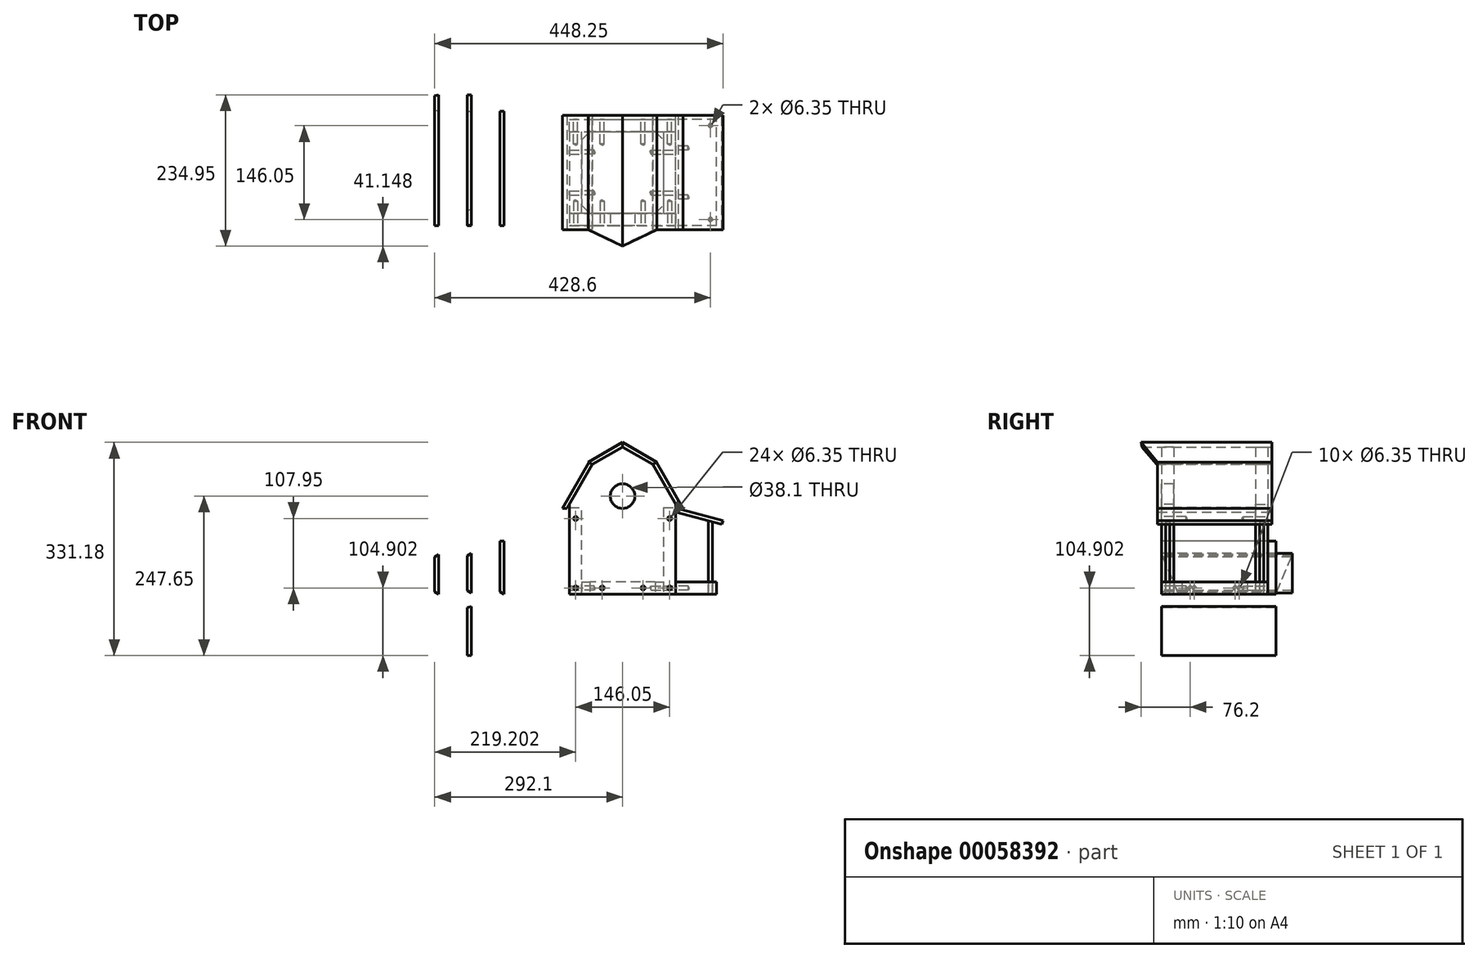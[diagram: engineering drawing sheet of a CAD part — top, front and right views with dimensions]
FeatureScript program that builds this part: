
annotation { "Feature Type Name" : "Feature", "Feature Type Description" : "" }
export const myFeature = defineFeature(function(context is Context, id is Id, definition is map)
    precondition{}
    {
        {
            var Q0;
            Q0=qCreatedBy(makeId("Front.planeOp"),FACE);
            var sketch = newSketch(context, id + "F0", { "sketchPlane" : qUnion([Q0])});
            skLineSegment(sketch, "E0", {"start": v(0, 0) * mm, "end": v(0, 139.7) * mm});
            skLineSegment(sketch, "E1", {"start": v(0, 139.7) * mm, "end": v(35.71, 201.56) * mm});
            skLineSegment(sketch, "E2", {"start": v(35.71, 201.56) * mm, "end": v(82.55, 228.6) * mm});
            skLineSegment(sketch, "E3", {"start": v(129.39, 201.56) * mm, "end": v(165.1, 139.7) * mm});
            skLineSegment(sketch, "E4", {"start": v(165.1, 139.7) * mm, "end": v(165.1, 0) * mm});
            skLineSegment(sketch, "E5", {"start": v(165.1, 0) * mm, "end": v(0, 0) * mm});
            skLineSegment(sketch, "E6", {"start": v(82.55, 0) * mm, "end": v(82.55, 304.8) * mm, "construction": true});
            skLineSegment(sketch, "E7", {"start": v(82.55, 228.6) * mm, "end": v(129.39, 201.56) * mm});
            skLineSegment(sketch, "E8", {"start": v(-28.74, 228.6) * mm, "end": v(153.15, 228.6) * mm, "construction": true});
            skCircle(sketch, "E9", {"center": v(82.55, 152.4) * mm, "radius": 19.05 * mm});
            skCircle(sketch, "E10", {"center": v(9.65, 9.65) * mm, "radius": 3.18 * mm});
            skCircle(sketch, "E11", {"center": v(50.8, 9.65) * mm, "radius": 3.17 * mm});
            skCircle(sketch, "E12", {"center": v(114.43, 9.65) * mm, "radius": 3.18 * mm});
            skCircle(sketch, "E13", {"center": v(155.7, 9.65) * mm, "radius": 3.18 * mm});
            skCircle(sketch, "E14", {"center": v(9.65, 117.6) * mm, "radius": 3.18 * mm});
            skCircle(sketch, "E15", {"center": v(155.7, 117.6) * mm, "radius": 3.18 * mm});
            skLineSegment(sketch, "E16.bottom", {"start": v(9.65, 9.65) * mm, "end": v(155.7, 9.65) * mm, "construction": true});
            skLineSegment(sketch, "E16.top", {"start": v(9.65, 117.6) * mm, "end": v(155.7, 117.6) * mm, "construction": true});
            skLineSegment(sketch, "E16.left", {"start": v(9.65, 9.65) * mm, "end": v(9.65, 117.6) * mm, "construction": true});
            skLineSegment(sketch, "E16.right", {"start": v(155.7, 9.65) * mm, "end": v(155.7, 117.6) * mm, "construction": true});
            skSolve(sketch);
        }
        {
            var Q0;
            Q0=makeQuery(id+"F0.imprint","IMPRINT",FACE,{"disambiguationData":[TD([[makeQuery(id+"F0.imprint","IMPRINT",EDGE,{"derivedFrom":sQuery(id+"F0.wireOp",EDGE,"E0")}),-1.0]])]});
            extrude(context, id + "F1", {"entities" : qUnion([Q0]), "oppositeDirection" : true, "depth" : 19.05 * mm});
        }
        {
            var Q0;
            Q0=makeQuery(id+"F1.opExtrude","SWEPT_EDGE",EDGE,{"disambiguationData":[OSD([sQuery(id+"F0.wireOp",EDGE,"E2"),sQuery(id+"F0.wireOp",EDGE,"E7")])]});
            cPlane(context, id + "F2", {"entities" : qUnion([Q0]), "cplaneType" : CPlaneType.LINE_ANGLE, "offset" : 152.4 * mm, "angle" : 90 * degree, "width" : 152.4 * mm, "height" : 152.4 * mm});
        }
        {
            var Q0;
            Q0=qCreatedBy(makeId("Front.planeOp"),FACE);
            cPlane(context, id + "F3", {"entities" : qUnion([Q0]), "cplaneType" : CPlaneType.OFFSET, "offset" : 165.1 * mm, "oppositeDirection" : true, "width" : 152.4 * mm, "height" : 152.4 * mm});
        }
        {
            var Q0;
            Q0=qCreatedBy(id+"F3.planeOp",FACE);
            var sketch = newSketch(context, id + "F4", { "sketchPlane" : qUnion([Q0])});
            skLineSegment(sketch, "E17", {"start": v(0, 0) * mm, "end": v(0, 139.7) * mm});
            skLineSegment(sketch, "E18", {"start": v(0, 139.7) * mm, "end": v(35.71, 201.56) * mm});
            skLineSegment(sketch, "E19", {"start": v(35.71, 201.56) * mm, "end": v(82.55, 228.6) * mm});
            skLineSegment(sketch, "E20", {"start": v(82.55, 228.6) * mm, "end": v(129.39, 201.56) * mm});
            skLineSegment(sketch, "E21", {"start": v(129.39, 201.56) * mm, "end": v(165.1, 139.7) * mm});
            skLineSegment(sketch, "E22", {"start": v(0, 0) * mm, "end": v(165.1, 0) * mm});
            skLineSegment(sketch, "E23", {"start": v(165.1, 139.7) * mm, "end": v(165.1, 0) * mm});
            skCircle(sketch, "E24", {"center": v(9.65, 9.65) * mm, "radius": 3.18 * mm});
            skCircle(sketch, "E25", {"center": v(50.8, 9.65) * mm, "radius": 3.18 * mm});
            skCircle(sketch, "E26", {"center": v(114.43, 9.65) * mm, "radius": 3.18 * mm});
            skCircle(sketch, "E27", {"center": v(155.7, 9.65) * mm, "radius": 3.18 * mm});
            skCircle(sketch, "E28", {"center": v(155.7, 117.6) * mm, "radius": 3.18 * mm});
            skCircle(sketch, "E29", {"center": v(9.65, 117.6) * mm, "radius": 3.18 * mm});
            skLineSegment(sketch, "E30.bottom", {"start": v(155.7, 9.65) * mm, "end": v(9.65, 9.65) * mm, "construction": true});
            skLineSegment(sketch, "E30.top", {"start": v(155.7, 117.6) * mm, "end": v(9.65, 117.6) * mm, "construction": true});
            skLineSegment(sketch, "E30.left", {"start": v(155.7, 9.65) * mm, "end": v(155.7, 117.6) * mm, "construction": true});
            skLineSegment(sketch, "E30.right", {"start": v(9.65, 9.65) * mm, "end": v(9.65, 117.6) * mm, "construction": true});
            skSolve(sketch);
        }
        {
            var Q0;
            Q0=makeQuery(id+"F4.imprint","IMPRINT",FACE,{"disambiguationData":[TD([[makeQuery(id+"F4.imprint","IMPRINT",EDGE,{"derivedFrom":sQuery(id+"F4.wireOp",EDGE,"E17")}),-1.0]])]});
            extrude(context, id + "F5", {"entities" : qUnion([Q0]), "depth" : 19.05 * mm});
        }
        {
            var Q0;
            Q0=qCreatedBy(makeId("Top.planeOp"),FACE);
            var sketch = newSketch(context, id + "F6", { "sketchPlane" : qUnion([Q0])});
            skLineSegment(sketch, "E31", {"start": v(19.05, 133.35) * mm, "end": v(19.05, 31.75) * mm});
            skLineSegment(sketch, "E32", {"start": v(146.05, 133.35) * mm, "end": v(146.05, 31.75) * mm});
            skLineSegment(sketch, "E33", {"start": v(82.55, -58.96) * mm, "end": v(82.55, 162.28) * mm, "construction": true});
            skLineSegment(sketch, "E34", {"start": v(133.35, 19.05) * mm, "end": v(31.75, 19.05) * mm});
            skLineSegment(sketch, "E35", {"start": v(133.35, 146.05) * mm, "end": v(31.75, 146.05) * mm});
            skLineSegment(sketch, "E36", {"start": v(19.05, 31.75) * mm, "end": v(31.75, 19.05) * mm});
            skLineSegment(sketch, "E37", {"start": v(133.35, 19.05) * mm, "end": v(146.05, 31.75) * mm});
            skLineSegment(sketch, "E38", {"start": v(133.35, 146.05) * mm, "end": v(146.05, 133.35) * mm});
            skLineSegment(sketch, "E39", {"start": v(19.05, 133.35) * mm, "end": v(31.75, 146.05) * mm});
            skSolve(sketch);
        }
        {
            var Q0;
            Q0=makeQuery(id+"F6.imprint","IMPRINT",FACE,{"disambiguationData":[TD([[makeQuery(id+"F6.imprint","IMPRINT",EDGE,{"derivedFrom":sQuery(id+"F6.wireOp",EDGE,"E31")}),1.0]])]});
            var Q1;
            Q1=makeQuery(id+"F5.opExtrude","SWEPT_FACE",FACE,{"disambiguationData":[OSD([sQuery(id+"F4.wireOp",EDGE,"E22")])]});
            extrude(context, id + "F7", {"entities" : qUnion([Q0]), "endBoundEntityFace" : qUnion([Q1]), "depth" : 19.05 * mm});
        }
        {
            var Q0;
            Q0=makeQuery(id+"F7.opExtrude","SWEPT_FACE",FACE,{"disambiguationData":[OSD([sQuery(id+"F6.wireOp",EDGE,"E32")])]});
            var sketch = newSketch(context, id + "F8", { "sketchPlane" : qUnion([Q0])});
            skPoint(sketch, "E40", {"position": v(50.8, 9.65) * mm});
            skPoint(sketch, "E41", {"position": v(114.3, 9.65) * mm});
            skSolve(sketch);
        }
        {
            var Q0;
            Q0=makeQuery(id+"F7.opExtrude","SWEPT_FACE",FACE,{"disambiguationData":[OSD([sQuery(id+"F6.wireOp",EDGE,"E34")])]});
            var sketch = newSketch(context, id + "F9", { "sketchPlane" : qUnion([Q0])});
            skPoint(sketch, "E42", {"position": v(50.8, 9.65) * mm});
            skPoint(sketch, "E43", {"position": v(114.3, 9.65) * mm});
            skSolve(sketch);
        }
        {
            var Q0;
            Q0=makeQuery(id+"F7.opExtrude","SWEPT_FACE",FACE,{"disambiguationData":[OSD([sQuery(id+"F6.wireOp",EDGE,"E31")])]});
            var sketch = newSketch(context, id + "F10", { "sketchPlane" : qUnion([Q0])});
            skPoint(sketch, "E44", {"position": v(-114.3, 9.65) * mm});
            skPoint(sketch, "E45", {"position": v(-50.8, 9.65) * mm});
            skSolve(sketch);
        }
        {
            var Q0;
            Q0=makeQuery(id+"F7.opExtrude","SWEPT_FACE",FACE,{"disambiguationData":[OSD([sQuery(id+"F6.wireOp",EDGE,"E35")])]});
            var sketch = newSketch(context, id + "F11", { "sketchPlane" : qUnion([Q0])});
            skPoint(sketch, "E46", {"position": v(-114.3, 9.65) * mm});
            skPoint(sketch, "E47", {"position": v(-50.8, 9.65) * mm});
            skSolve(sketch);
        }
        {
            var Q0;
            Q0=sQuery(id+"F11.wireOp",VERTEX,"E46");
            var Q1;
            Q1=sQuery(id+"F11.wireOp",VERTEX,"E47");
            var Q2;
            Q2=sQuery(id+"F10.wireOp",VERTEX,"E44");
            var Q3;
            Q3=sQuery(id+"F10.wireOp",VERTEX,"E45");
            var Q4;
            Q4=sQuery(id+"F9.wireOp",VERTEX,"E42");
            var Q5;
            Q5=sQuery(id+"F9.wireOp",VERTEX,"E43");
            var Q6;
            Q6=sQuery(id+"F8.wireOp",VERTEX,"E40");
            var Q7;
            Q7=sQuery(id+"F8.wireOp",VERTEX,"E41");
            var Q8;
            Q8=makeQuery(id+"F7.opExtrude","SWEPT_BODY",BODY,{"disambiguationData":[OSD([sQuery(id+"F6.wireOp",EDGE,"E31"),sQuery(id+"F6.wireOp",EDGE,"E32"),sQuery(id+"F6.wireOp",EDGE,"E34"),sQuery(id+"F6.wireOp",EDGE,"E35"),sQuery(id+"F6.wireOp",EDGE,"E36"),sQuery(id+"F6.wireOp",EDGE,"E37"),sQuery(id+"F6.wireOp",EDGE,"E38"),sQuery(id+"F6.wireOp",EDGE,"E39")])]});
            hole(context, id + "F12", {"style" : HoleStyle.SIMPLE, "holeDiameter" : 6.35 * mm, "endStyle" : HoleEndStyle.BLIND, "holeDepth" : 19.05 * mm, "locations" : qUnion([Q0, Q1, Q2, Q3, Q4, Q5, Q6, Q7]), "scope" : qUnion([Q8])});
        }
        {
            var Q0;
            Q0=qCreatedBy(makeId("Right.planeOp"),FACE);
            cPlane(context, id + "F13", {"entities" : qUnion([Q0]), "cplaneType" : CPlaneType.OFFSET, "offset" : 165.1 * mm, "width" : 152.4 * mm, "height" : 152.4 * mm});
        }
        {
            var Q0;
            Q0=qCreatedBy(id+"F13.planeOp",FACE);
            var sketch = newSketch(context, id + "F14", { "sketchPlane" : qUnion([Q0])});
            skLineSegment(sketch, "E48.bottom", {"start": v(19.05, 0) * mm, "end": v(146.05, 0) * mm});
            skLineSegment(sketch, "E48.top", {"start": v(19.05, 134.87) * mm, "end": v(146.05, 134.87) * mm});
            skLineSegment(sketch, "E48.left", {"start": v(19.05, 0) * mm, "end": v(19.05, 134.87) * mm});
            skLineSegment(sketch, "E48.right", {"start": v(146.05, 0) * mm, "end": v(146.05, 134.87) * mm});
            skCircle(sketch, "E49", {"center": v(50.8, 9.65) * mm, "radius": 3.18 * mm});
            skCircle(sketch, "E50", {"center": v(114.3, 9.65) * mm, "radius": 3.18 * mm});
            skLineSegment(sketch, "E51", {"start": v(-9.39, 9.65) * mm, "end": v(175.82, 9.65) * mm, "construction": true});
            skSolve(sketch);
        }
        {
            var Q0;
            Q0=makeQuery(id+"F14.imprint","IMPRINT",FACE,{"disambiguationData":[TD([[makeQuery(id+"F14.imprint","IMPRINT",EDGE,{"derivedFrom":sQuery(id+"F14.wireOp",EDGE,"E48.bottom")}),1.0]])]});
            var Q1;
            Q1=makeQuery(id+"F7.opExtrude","SWEPT_FACE",FACE,{"disambiguationData":[OSD([sQuery(id+"F6.wireOp",EDGE,"E32")])]});
            extrude(context, id + "F15", {"entities" : qUnion([Q0]), "endBound" : BoundingType.UP_TO_SURFACE, "oppositeDirection" : true, "endBoundEntityFace" : qUnion([Q1]), "depth" : 25.4 * mm});
        }
        {
            var Q0;
            Q0=makeQuery(id+"F15.opExtrude","SWEPT_BODY",BODY,{"disambiguationData":[OSD([sQuery(id+"F14.wireOp",EDGE,"E48.bottom"),sQuery(id+"F14.wireOp",EDGE,"E48.top"),sQuery(id+"F14.wireOp",EDGE,"E48.left"),sQuery(id+"F14.wireOp",EDGE,"E48.right")])]});
            transform(context, id + "F16", {"entities" : qUnion([Q0]), "transformType" : TransformType.TRANSLATION_3D, "dx" : -146.05 * mm, "dy" : 0 * mm, "dz" : 0 * mm, "makeCopy" : true});
        }
        {
            var Q0;
            Q0=makeQuery(id+"F15.opExtrude","SWEPT_FACE",FACE,{"disambiguationData":[OSD([sQuery(id+"F14.wireOp",EDGE,"E48.left")])]});
            var sketch = newSketch(context, id + "F17", { "sketchPlane" : qUnion([Q0])});
            skPoint(sketch, "E52", {"position": v(155.45, 117.6) * mm});
            skPoint(sketch, "E53", {"position": v(9.65, 117.6) * mm});
            skPoint(sketch, "E54", {"position": v(9.65, 9.65) * mm});
            skPoint(sketch, "E55", {"position": v(155.45, 9.65) * mm});
            skSolve(sketch);
        }
        {
            var Q0;
            Q0=sQuery(id+"F17.wireOp",VERTEX,"E53");
            var Q1;
            Q1=sQuery(id+"F17.wireOp",VERTEX,"E52");
            var Q2;
            Q2=sQuery(id+"F17.wireOp",VERTEX,"E54");
            var Q3;
            Q3=sQuery(id+"F17.wireOp",VERTEX,"E55");
            var Q4;
            Q4=makeQuery(id+"F16.opPattern","COPY",BODY,{"derivedFrom":makeQuery(id+"F15.opExtrude","SWEPT_BODY",BODY,{"disambiguationData":[OSD([sQuery(id+"F14.wireOp",EDGE,"E48.bottom"),sQuery(id+"F14.wireOp",EDGE,"E48.top"),sQuery(id+"F14.wireOp",EDGE,"E48.left"),sQuery(id+"F14.wireOp",EDGE,"E48.right"),sQuery(id+"F14.wireOp",EDGE,"E49"),sQuery(id+"F14.wireOp",EDGE,"E50")])]}),"instanceName":"1"});
            var Q5;
            Q5=makeQuery(id+"F15.opExtrude","SWEPT_BODY",BODY,{"disambiguationData":[OSD([sQuery(id+"F14.wireOp",EDGE,"E48.bottom"),sQuery(id+"F14.wireOp",EDGE,"E48.top"),sQuery(id+"F14.wireOp",EDGE,"E48.left"),sQuery(id+"F14.wireOp",EDGE,"E48.right"),sQuery(id+"F14.wireOp",EDGE,"E49"),sQuery(id+"F14.wireOp",EDGE,"E50")])]});
            hole(context, id + "F18", {"style" : HoleStyle.SIMPLE, "holeDiameter" : 6.35 * mm, "endStyle" : HoleEndStyle.BLIND, "holeDepth" : 19.05 * mm, "locations" : qUnion([Q0, Q1, Q2, Q3]), "scope" : qUnion([Q4, Q5])});
        }
        {
            var Q0;
            Q0=makeQuery(id+"F15.opExtrude","SWEPT_FACE",FACE,{"disambiguationData":[OSD([sQuery(id+"F14.wireOp",EDGE,"E48.right")])]});
            var sketch = newSketch(context, id + "F19", { "sketchPlane" : qUnion([Q0])});
            skPoint(sketch, "E56", {"position": v(-155.45, 117.6) * mm});
            skPoint(sketch, "E57", {"position": v(-9.65, 117.6) * mm});
            skPoint(sketch, "E58", {"position": v(-9.65, 9.65) * mm});
            skPoint(sketch, "E59", {"position": v(-155.45, 9.65) * mm});
            skSolve(sketch);
        }
        {
            var Q0;
            Q0=sQuery(id+"F19.wireOp",VERTEX,"E56");
            var Q1;
            Q1=sQuery(id+"F19.wireOp",VERTEX,"E57");
            var Q2;
            Q2=sQuery(id+"F19.wireOp",VERTEX,"E58");
            var Q3;
            Q3=sQuery(id+"F19.wireOp",VERTEX,"E59");
            var Q4;
            Q4=makeQuery(id+"F15.opExtrude","SWEPT_BODY",BODY,{"disambiguationData":[OSD([sQuery(id+"F14.wireOp",EDGE,"E48.bottom"),sQuery(id+"F14.wireOp",EDGE,"E48.top"),sQuery(id+"F14.wireOp",EDGE,"E48.left"),sQuery(id+"F14.wireOp",EDGE,"E48.right"),sQuery(id+"F14.wireOp",EDGE,"E49"),sQuery(id+"F14.wireOp",EDGE,"E50")])]});
            var Q5;
            Q5=makeQuery(id+"F16.opPattern","COPY",BODY,{"derivedFrom":makeQuery(id+"F15.opExtrude","SWEPT_BODY",BODY,{"disambiguationData":[OSD([sQuery(id+"F14.wireOp",EDGE,"E48.bottom"),sQuery(id+"F14.wireOp",EDGE,"E48.top"),sQuery(id+"F14.wireOp",EDGE,"E48.left"),sQuery(id+"F14.wireOp",EDGE,"E48.right"),sQuery(id+"F14.wireOp",EDGE,"E49"),sQuery(id+"F14.wireOp",EDGE,"E50")])]}),"instanceName":"1"});
            hole(context, id + "F20", {"style" : HoleStyle.SIMPLE, "holeDiameter" : 6.35 * mm, "endStyle" : HoleEndStyle.BLIND, "holeDepth" : 19.05 * mm, "locations" : qUnion([Q0, Q1, Q2, Q3]), "scope" : qUnion([Q4, Q5])});
        }
        {
            var Q0;
            Q0=makeQuery(id+"F1.opExtrude","CAP_FACE",FACE,{"disambiguationData":[OSD([sQuery(id+"F0.wireOp",EDGE,"E0"),sQuery(id+"F0.wireOp",EDGE,"E1"),sQuery(id+"F0.wireOp",EDGE,"E2"),sQuery(id+"F0.wireOp",EDGE,"E3"),sQuery(id+"F0.wireOp",EDGE,"E4"),sQuery(id+"F0.wireOp",EDGE,"E5"),sQuery(id+"F0.wireOp",EDGE,"E7"),sQuery(id+"F0.wireOp",EDGE,"E9")])],"isStart":true});
            var sketch = newSketch(context, id + "F21", { "sketchPlane" : qUnion([Q0])});
            skLineSegment(sketch, "E60", {"start": v(82.55, 228.6) * mm, "end": v(82.55, 235.93) * mm});
            skLineSegment(sketch, "E61", {"start": v(135.74, 205.23) * mm, "end": v(129.39, 201.56) * mm});
            skLineSegment(sketch, "E62", {"start": v(129.39, 201.56) * mm, "end": v(82.55, 228.6) * mm});
            skLineSegment(sketch, "E63", {"start": v(82.55, 235.93) * mm, "end": v(135.74, 205.23) * mm});
            skSolve(sketch);
        }
        {
            var Q0;
            Q0=makeQuery(id+"F21.imprint","IMPRINT",FACE,{"disambiguationData":[TD([[makeQuery(id+"F21.imprint","IMPRINT",EDGE,{"derivedFrom":sQuery(id+"F21.wireOp",EDGE,"E60")}),-1.0]])]});
            extrude(context, id + "F22", {"entities" : qUnion([Q0]), "depth" : 31.75 * mm, "hasSecondDirection" : true, "secondDirectionOppositeDirection" : true, "secondDirectionDepth" : 171.45 * mm});
        }
        {
            var Q0;
            Q0=makeQuery(id+"F22.opExtrude","SWEPT_FACE",FACE,{"disambiguationData":[OSD([sQuery(id+"F21.wireOp",EDGE,"E63")])]});
            var sketch = newSketch(context, id + "F23", { "sketchPlane" : qUnion([Q0])});
            skLineSegment(sketch, "E64", {"start": v(-46.48, -31.75) * mm, "end": v(14.94, -31.75) * mm});
            skLineSegment(sketch, "E65", {"start": v(14.94, -31.75) * mm, "end": v(14.94, -6.31) * mm});
            skLineSegment(sketch, "E66", {"start": v(14.94, -6.31) * mm, "end": v(-46.48, -31.75) * mm});
            skSolve(sketch);
        }
        {
            var Q0;
            Q0=makeQuery(id+"F23.imprint","IMPRINT",FACE,{"disambiguationData":[TD([[makeQuery(id+"F23.imprint","IMPRINT",EDGE,{"derivedFrom":sQuery(id+"F23.wireOp",EDGE,"E64")}),1.0]])]});
            extrude(context, id + "F24", {"entities" : qUnion([Q0]), "operationType" : NewBodyOperationType.REMOVE, "oppositeDirection" : true, "depth" : 25.4 * mm});
        }
        {
            var Q0;
            Q0=makeQuery(id+"F22.opExtrude","SWEPT_BODY",BODY,{"disambiguationData":[OSD([sQuery(id+"F21.wireOp",EDGE,"E60"),sQuery(id+"F21.wireOp",EDGE,"E61"),sQuery(id+"F21.wireOp",EDGE,"E62"),sQuery(id+"F21.wireOp",EDGE,"E63")])]});
            var Q1;
            Q1=qCreatedBy(id+"F2.planeOp",FACE);
            mirror(context, id + "F25", {"entities" : qUnion([Q0]), "mirrorPlane" : qUnion([Q1])});
        }
        {
            var Q0;
            Q0=makeQuery(id+"F1.opExtrude","CAP_FACE",FACE,{"disambiguationData":[OSD([sQuery(id+"F0.wireOp",EDGE,"E0"),sQuery(id+"F0.wireOp",EDGE,"E1"),sQuery(id+"F0.wireOp",EDGE,"E2"),sQuery(id+"F0.wireOp",EDGE,"E3"),sQuery(id+"F0.wireOp",EDGE,"E4"),sQuery(id+"F0.wireOp",EDGE,"E5"),sQuery(id+"F0.wireOp",EDGE,"E7"),sQuery(id+"F0.wireOp",EDGE,"E9"),sQuery(id+"F0.wireOp",EDGE,"E10"),sQuery(id+"F0.wireOp",EDGE,"E11"),sQuery(id+"F0.wireOp",EDGE,"E12"),sQuery(id+"F0.wireOp",EDGE,"E13"),sQuery(id+"F0.wireOp",EDGE,"E14"),sQuery(id+"F0.wireOp",EDGE,"E15")])],"isStart":true});
            var sketch = newSketch(context, id + "F26", { "sketchPlane" : qUnion([Q0])});
            skLineSegment(sketch, "E67", {"start": v(134.88, 204.73) * mm, "end": v(129.39, 201.56) * mm});
            skLineSegment(sketch, "E68", {"start": v(129.39, 201.56) * mm, "end": v(168.83, 133.24) * mm});
            skLineSegment(sketch, "E69", {"start": v(176.16, 133.24) * mm, "end": v(134.88, 204.73) * mm});
            skLineSegment(sketch, "E70", {"start": v(176.16, 133.24) * mm, "end": v(168.83, 133.24) * mm});
            skSolve(sketch);
        }
        {
            var Q0;
            Q0=makeQuery(id+"F26.imprint","IMPRINT",FACE,{"disambiguationData":[TD([[makeQuery(id+"F26.imprint","IMPRINT",EDGE,{"derivedFrom":sQuery(id+"F26.wireOp",EDGE,"E67")}),1.0]])]});
            var Q1;
            Q1=makeQuery(id+"F22.opExtrude","CAP_FACE",FACE,{"disambiguationData":[OSD([sQuery(id+"F21.wireOp",EDGE,"E60"),sQuery(id+"F21.wireOp",EDGE,"E61"),sQuery(id+"F21.wireOp",EDGE,"E62"),sQuery(id+"F21.wireOp",EDGE,"E63")])],"isStart":true});
            extrude(context, id + "F27", {"entities" : qUnion([Q0]), "oppositeDirection" : true, "endBoundEntityFace" : qUnion([Q1]), "depth" : 171.45 * mm, "hasSecondDirection" : true, "secondDirectionOppositeDirection" : false, "secondDirectionDepth" : 6.35 * mm});
        }
        {
            var Q0;
            Q0=makeQuery(id+"F27.opExtrude","SWEPT_BODY",BODY,{"disambiguationData":[OSD([sQuery(id+"F26.wireOp",EDGE,"E67"),sQuery(id+"F26.wireOp",EDGE,"E68"),sQuery(id+"F26.wireOp",EDGE,"6fb6b2ac-7d98-48f0-bfc0-cfe1588ae646"),sQuery(id+"F26.wireOp",EDGE,"E69")])]});
            var Q1;
            Q1=qCreatedBy(id+"F2.planeOp",FACE);
            mirror(context, id + "F28", {"entities" : qUnion([Q0]), "mirrorPlane" : qUnion([Q1])});
        }
        {
            var Q0;
            Q0=qCreatedBy(makeId("Right.planeOp"),FACE);
            cPlane(context, id + "F29", {"entities" : qUnion([Q0]), "cplaneType" : CPlaneType.OFFSET, "offset" : 165.2 * mm, "width" : 152.4 * mm, "height" : 152.4 * mm});
        }
        {
            var Q0;
            Q0=qCreatedBy(id+"F29.planeOp",FACE);
            var sketch = newSketch(context, id + "F30", { "sketchPlane" : qUnion([Q0])});
            skLineSegment(sketch, "E71.bottom", {"start": v(0, 0) * mm, "end": v(165.1, 0) * mm});
            skLineSegment(sketch, "E71.top", {"start": v(0, 19.05) * mm, "end": v(165.1, 19.05) * mm});
            skLineSegment(sketch, "E71.left", {"start": v(0, 0) * mm, "end": v(0, 19.05) * mm});
            skLineSegment(sketch, "E71.right", {"start": v(165.1, 0) * mm, "end": v(165.1, 19.05) * mm});
            skSolve(sketch);
        }
        {
            var Q0;
            Q0=makeQuery(id+"F30.imprint","IMPRINT",FACE,{"disambiguationData":[TD([[makeQuery(id+"F30.imprint","IMPRINT",EDGE,{"derivedFrom":sQuery(id+"F30.wireOp",EDGE,"E71.bottom")}),1.0]])]});
            extrude(context, id + "F31", {"entities" : qUnion([Q0]), "depth" : 63.5 * mm});
        }
        {
            var Q0;
            Q0=makeQuery(id+"F31.opExtrude","CAP_FACE",FACE,{"disambiguationData":[OSD([sQuery(id+"F30.wireOp",EDGE,"E71.bottom"),sQuery(id+"F30.wireOp",EDGE,"E71.top"),sQuery(id+"F30.wireOp",EDGE,"E71.left"),sQuery(id+"F30.wireOp",EDGE,"E71.right")])],"isStart":true});
            var sketch = newSketch(context, id + "F32", { "sketchPlane" : qUnion([Q0])});
            skPoint(sketch, "E72", {"position": v(-44.45, 9.65) * mm});
            skPoint(sketch, "E73", {"position": v(-120.65, 9.65) * mm});
            skSolve(sketch);
        }
        {
            var Q0;
            Q0=sQuery(id+"F32.wireOp",VERTEX,"E73");
            var Q1;
            Q1=sQuery(id+"F32.wireOp",VERTEX,"E72");
            var Q2;
            Q2=makeQuery(id+"F31.opExtrude","SWEPT_BODY",BODY,{"disambiguationData":[OSD([sQuery(id+"F30.wireOp",EDGE,"E71.bottom"),sQuery(id+"F30.wireOp",EDGE,"E71.top"),sQuery(id+"F30.wireOp",EDGE,"E71.left"),sQuery(id+"F30.wireOp",EDGE,"E71.right")])]});
            hole(context, id + "F33", {"style" : HoleStyle.SIMPLE, "holeDiameter" : 6.35 * mm, "endStyle" : HoleEndStyle.BLIND, "holeDepth" : 19.05 * mm, "locations" : qUnion([Q0, Q1]), "scope" : qUnion([Q2])});
        }
        {
            var Q0;
            Q0=makeQuery(id+"F31.opExtrude","SWEPT_FACE",FACE,{"disambiguationData":[OSD([sQuery(id+"F30.wireOp",EDGE,"E71.top")])]});
            var sketch = newSketch(context, id + "F34", { "sketchPlane" : qUnion([Q0])});
            skPoint(sketch, "E74", {"position": v(219.05, 155.45) * mm});
            skPoint(sketch, "E75", {"position": v(219.05, 9.4) * mm});
            skSolve(sketch);
        }
        {
            var Q0;
            Q0=sQuery(id+"F34.wireOp",VERTEX,"E74");
            var Q1;
            Q1=sQuery(id+"F34.wireOp",VERTEX,"E75");
            var Q2;
            Q2=makeQuery(id+"F31.opExtrude","SWEPT_BODY",BODY,{"disambiguationData":[OSD([sQuery(id+"F30.wireOp",EDGE,"E71.bottom"),sQuery(id+"F30.wireOp",EDGE,"E71.top"),sQuery(id+"F30.wireOp",EDGE,"E71.left"),sQuery(id+"F30.wireOp",EDGE,"E71.right")])]});
            hole(context, id + "F35", {"style" : HoleStyle.SIMPLE, "holeDiameter" : 6.35 * mm, "endStyle" : HoleEndStyle.THROUGH, "locations" : qUnion([Q0, Q1]), "scope" : qUnion([Q2])});
        }
        {
            var Q0;
            Q0=qCreatedBy(makeId("Front.planeOp"),FACE);
            var sketch = newSketch(context, id + "F36", { "sketchPlane" : qUnion([Q0])});
            skLineSegment(sketch, "E76", {"start": v(165.1, 134.11) * mm, "end": v(238.7, 114.39) * mm});
            skLineSegment(sketch, "E77", {"start": v(238.7, 114.39) * mm, "end": v(237.06, 108.26) * mm});
            skLineSegment(sketch, "E78", {"start": v(237.06, 108.26) * mm, "end": v(165.1, 127.54) * mm});
            skLineSegment(sketch, "E79", {"start": v(165.1, 127.54) * mm, "end": v(165.1, 134.11) * mm});
            skSolve(sketch);
        }
        {
            var Q0;
            Q0=makeQuery(id+"F36.imprint","IMPRINT",FACE,{"disambiguationData":[TD([[makeQuery(id+"F36.imprint","IMPRINT",EDGE,{"derivedFrom":sQuery(id+"F36.wireOp",EDGE,"E76")}),-1.0]])]});
            var Q1;
            Q1=makeQuery(id+"F27.opExtrude","CAP_FACE",FACE,{"disambiguationData":[OSD([sQuery(id+"F26.wireOp",EDGE,"E67"),sQuery(id+"F26.wireOp",EDGE,"E68"),sQuery(id+"F26.wireOp",EDGE,"6fb6b2ac-7d98-48f0-bfc0-cfe1588ae646"),sQuery(id+"F26.wireOp",EDGE,"E69")])],"isStart":true});
            var Q2;
            Q2=makeQuery(id+"F27.opExtrude","CAP_FACE",FACE,{"disambiguationData":[OSD([sQuery(id+"F26.wireOp",EDGE,"E67"),sQuery(id+"F26.wireOp",EDGE,"E68"),sQuery(id+"F26.wireOp",EDGE,"6fb6b2ac-7d98-48f0-bfc0-cfe1588ae646"),sQuery(id+"F26.wireOp",EDGE,"E69")])],"isStart":false});
            extrude(context, id + "F37", {"entities" : qUnion([Q0]), "endBound" : BoundingType.UP_TO_SURFACE, "endBoundEntityFace" : qUnion([Q1]), "depth" : 25.4 * mm, "hasSecondDirection" : true, "secondDirectionBound" : SecondDirectionBoundingType.UP_TO_SURFACE, "secondDirectionOppositeDirection" : true, "secondDirectionBoundEntityFace" : qUnion([Q2]), "secondDirectionDepth" : 25.4 * mm});
        }
        {
            var Q0;
            Q0=makeQuery(id+"F31.opExtrude","SWEPT_FACE",FACE,{"disambiguationData":[OSD([sQuery(id+"F30.wireOp",EDGE,"E71.bottom")])]});
            var sketch = newSketch(context, id + "F38", { "sketchPlane" : qUnion([Q0])});
            skCircle(sketch, "E80", {"center": v(219.05, -155.7) * mm, "radius": 3.18 * mm});
            skCircle(sketch, "E81", {"center": v(219.05, -9.65) * mm, "radius": 3.18 * mm});
            skLineSegment(sketch, "E82", {"start": v(219.05, -41.77) * mm, "end": v(219.05, 168.5) * mm, "construction": true});
            skSolve(sketch);
        }
        {
            var Q0;
            Q0=makeQuery(id+"F38.imprint","IMPRINT",FACE,{"disambiguationData":[TD([[makeQuery(id+"F38.imprint","IMPRINT",EDGE,{"derivedFrom":sQuery(id+"F38.wireOp",EDGE,"E81")}),1.0]])]});
            var Q1;
            Q1=makeQuery(id+"F38.imprint","IMPRINT",FACE,{"disambiguationData":[TD([[makeQuery(id+"F38.imprint","IMPRINT",EDGE,{"derivedFrom":sQuery(id+"F38.wireOp",EDGE,"E80")}),1.0]])]});
            var Q2;
            Q2=makeQuery(id+"F37.opExtrude","SWEPT_FACE",FACE,{"disambiguationData":[OSD([sQuery(id+"F36.wireOp",EDGE,"E78")])]});
            extrude(context, id + "F39", {"entities" : qUnion([Q0, Q1]), "endBound" : BoundingType.UP_TO_SURFACE, "oppositeDirection" : true, "endBoundEntityFace" : qUnion([Q2]), "depth" : 25.4 * mm});
        }
        {
            var Q0;
            Q0=qCreatedBy(makeId("Front.planeOp"),FACE);
            var sketch = newSketch(context, id + "F40", { "sketchPlane" : qUnion([Q0])});
            skLineSegment(sketch, "E83", {"start": v(-152.4, 63.5) * mm, "end": v(-152.4, 2.07) * mm});
            skLineSegment(sketch, "E84", {"start": v(-152.4, 63.5) * mm, "end": v(-158.75, 59.83) * mm});
            skLineSegment(sketch, "E85", {"start": v(-158.75, 59.83) * mm, "end": v(-158.75, 5.73) * mm});
            skLineSegment(sketch, "E86", {"start": v(-158.75, 5.73) * mm, "end": v(-152.4, 2.07) * mm});
            skLineSegment(sketch, "E87", {"start": v(-124.49, 63.5) * mm, "end": v(-197.42, 63.5) * mm, "construction": true});
            skLineSegment(sketch, "E88", {"start": v(-124, 2.07) * mm, "end": v(-189.13, 2.07) * mm, "construction": true});
            skSolve(sketch);
        }
        {
            var Q0;
            Q0=makeQuery(id+"F40.imprint","IMPRINT",FACE,{"disambiguationData":[TD([[makeQuery(id+"F40.imprint","IMPRINT",EDGE,{"derivedFrom":sQuery(id+"F40.wireOp",EDGE,"E83")}),-1.0]])]});
            extrude(context, id + "F41", {"entities" : qUnion([Q0]), "oppositeDirection" : true, "depth" : 203.2 * mm});
        }
        {
            var Q0;
            Q0=makeQuery(id+"F41.opExtrude","SWEPT_FACE",FACE,{"disambiguationData":[OSD([sQuery(id+"F40.wireOp",EDGE,"E83")])]});
            var sketch = newSketch(context, id + "F42", { "sketchPlane" : qUnion([Q0])});
            skLineSegment(sketch, "E89", {"start": v(0, 63.5) * mm, "end": v(0, 2.07) * mm});
            skLineSegment(sketch, "E90", {"start": v(0, 2.07) * mm, "end": v(25.45, 2.07) * mm});
            skLineSegment(sketch, "E91", {"start": v(25.45, 2.07) * mm, "end": v(0, 63.5) * mm});
            skSolve(sketch);
        }
        {
            var Q0;
            Q0=makeQuery(id+"F42.imprint","IMPRINT",FACE,{"disambiguationData":[TD([[makeQuery(id+"F42.imprint","IMPRINT",EDGE,{"derivedFrom":sQuery(id+"F42.wireOp",EDGE,"E89")}),1.0]])]});
            extrude(context, id + "F43", {"entities" : qUnion([Q0]), "operationType" : NewBodyOperationType.REMOVE, "endBound" : BoundingType.THROUGH_ALL, "oppositeDirection" : true, "depth" : 6.35 * mm});
        }
        {
            var Q0;
            Q0=qCreatedBy(makeId("Front.planeOp"),FACE);
            var sketch = newSketch(context, id + "F44", { "sketchPlane" : qUnion([Q0])});
            skLineSegment(sketch, "E92", {"start": v(-203.2, 61.43) * mm, "end": v(-203.2, 0) * mm});
            skLineSegment(sketch, "E93", {"start": v(-203.2, 0) * mm, "end": v(-209.55, 3.67) * mm});
            skLineSegment(sketch, "E94", {"start": v(-209.55, 3.67) * mm, "end": v(-209.55, 57.77) * mm});
            skLineSegment(sketch, "E95", {"start": v(-209.55, 57.77) * mm, "end": v(-203.2, 61.43) * mm});
            skLineSegment(sketch, "E96", {"start": v(-185.94, 61.43) * mm, "end": v(-224.99, 61.43) * mm, "construction": true});
            skLineSegment(sketch, "E97", {"start": v(-191.62, 0) * mm, "end": v(-225.72, 0) * mm, "construction": true});
            skSolve(sketch);
        }
        {
            var Q0;
            Q0=makeQuery(id+"F44.imprint","IMPRINT",FACE,{"disambiguationData":[TD([[makeQuery(id+"F44.imprint","IMPRINT",EDGE,{"derivedFrom":sQuery(id+"F44.wireOp",EDGE,"E92")}),-1.0]])]});
            extrude(context, id + "F45", {"entities" : qUnion([Q0]), "oppositeDirection" : true, "depth" : 203.2 * mm});
        }
        {
            var Q0;
            Q0=makeQuery(id+"F45.opExtrude","SWEPT_FACE",FACE,{"disambiguationData":[OSD([sQuery(id+"F44.wireOp",EDGE,"E92")])]});
            var sketch = newSketch(context, id + "F46", { "sketchPlane" : qUnion([Q0])});
            skLineSegment(sketch, "E98", {"start": v(203.2, 61.43) * mm, "end": v(203.2, 0) * mm});
            skLineSegment(sketch, "E99", {"start": v(203.2, 0) * mm, "end": v(177.8, 0) * mm});
            skLineSegment(sketch, "E100", {"start": v(177.8, 0) * mm, "end": v(203.2, 61.43) * mm});
            skSolve(sketch);
        }
        {
            var Q0;
            Q0=makeQuery(id+"F46.imprint","IMPRINT",FACE,{"disambiguationData":[TD([[makeQuery(id+"F46.imprint","IMPRINT",EDGE,{"derivedFrom":sQuery(id+"F46.wireOp",EDGE,"E98")}),-1.0]])]});
            extrude(context, id + "F47", {"entities" : qUnion([Q0]), "operationType" : NewBodyOperationType.REMOVE, "endBound" : BoundingType.THROUGH_ALL, "oppositeDirection" : true, "depth" : 25.4 * mm});
        }
        {
            var Q0;
            Q0=qCreatedBy(makeId("Front.planeOp"),FACE);
            var sketch = newSketch(context, id + "F48", { "sketchPlane" : qUnion([Q0])});
            skLineSegment(sketch, "E101.bottom", {"start": v(-107.95, 0) * mm, "end": v(-101.6, 0) * mm, "construction": true});
            skLineSegment(sketch, "E101.top", {"start": v(-107.95, 82.55) * mm, "end": v(-101.6, 82.55) * mm});
            skLineSegment(sketch, "E101.left", {"start": v(-107.95, 3.67) * mm, "end": v(-107.95, 82.55) * mm});
            skLineSegment(sketch, "E101.right", {"start": v(-101.6, 0) * mm, "end": v(-101.6, 82.55) * mm});
            skLineSegment(sketch, "E102", {"start": v(-101.6, 0) * mm, "end": v(-107.95, 3.67) * mm});
            skSolve(sketch);
        }
        {
            var Q0;
            Q0=makeQuery(id+"F48.imprint","IMPRINT",FACE,{"disambiguationData":[TD([[makeQuery(id+"F48.imprint","IMPRINT",EDGE,{"derivedFrom":sQuery(id+"F48.wireOp",EDGE,"E101.top")}),-1.0]])]});
            extrude(context, id + "F49", {"entities" : qUnion([Q0]), "oppositeDirection" : true, "depth" : 177.8 * mm});
        }
        {
            var Q0;
            Q0=qCreatedBy(makeId("Front.planeOp"),FACE);
            var sketch = newSketch(context, id + "F50", { "sketchPlane" : qUnion([Q0])});
            skLineSegment(sketch, "E103", {"start": v(-152.4, -19.05) * mm, "end": v(-152.4, -95.25) * mm});
            skLineSegment(sketch, "E104", {"start": v(-152.4, -95.25) * mm, "end": v(-158.75, -95.25) * mm});
            skLineSegment(sketch, "E105", {"start": v(-158.75, -95.25) * mm, "end": v(-158.75, -20.75) * mm});
            skLineSegment(sketch, "E106", {"start": v(-158.75, -20.75) * mm, "end": v(-152.4, -19.05) * mm});
            skLineSegment(sketch, "E107", {"start": v(-127.28, -19.05) * mm, "end": v(-198.6, -19.05) * mm, "construction": true});
            skSolve(sketch);
        }
        {
            var Q0;
            Q0=makeQuery(id+"F50.imprint","IMPRINT",FACE,{"disambiguationData":[TD([[makeQuery(id+"F50.imprint","IMPRINT",EDGE,{"derivedFrom":sQuery(id+"F50.wireOp",EDGE,"E103")}),-1.0]])]});
            extrude(context, id + "F51", {"entities" : qUnion([Q0]), "oppositeDirection" : true, "depth" : 177.8 * mm});
        }
    });
